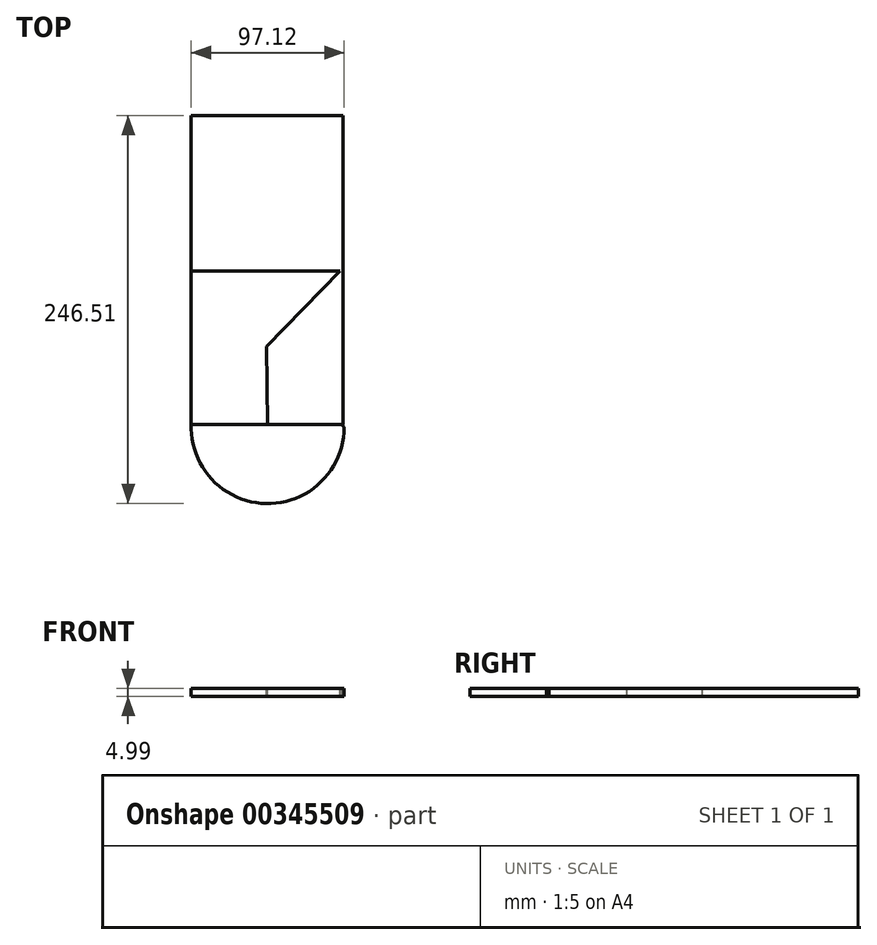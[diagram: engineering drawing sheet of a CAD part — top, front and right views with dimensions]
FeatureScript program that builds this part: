
annotation { "Feature Type Name" : "Feature", "Feature Type Description" : "" }
export const myFeature = defineFeature(function(context is Context, id is Id, definition is map)
    precondition{}
    {
        {
            var Q0;
            Q0=qCreatedBy(makeId("Top.planeOp"),FACE);
            var sketch = newSketch(context, id + "F0", { "sketchPlane" : qUnion([Q0])});
            skLineSegment(sketch, "E0.bottom", {"start": v(96.47, -97.42) * mm, "end": v(0, -97.42) * mm});
            skLineSegment(sketch, "E0.top", {"start": v(96.47, 98.96) * mm, "end": v(0, 98.96) * mm});
            skLineSegment(sketch, "E0.left", {"start": v(96.47, -97.42) * mm, "end": v(96.47, 98.96) * mm});
            skLineSegment(sketch, "E0.right", {"start": v(0, -97.42) * mm, "end": v(0, 98.96) * mm});
            skSolve(sketch);
        }
        {
            var Q0;
            Q0 = qSketchRegion(id + "F0", true);
            var sketch = newSketch(context, id + "F1", { "sketchPlane" : qUnion([Q0])});
            skArc(sketch, "E1", {"start": v(0, -96.81) * mm, "mid": v(0, -96.88) * mm, "end": v(0, -96.94) * mm});
            skLineSegment(sketch, "E2", {"start": v(94.51, 0) * mm, "end": v(0, 0) * mm});
            skLineSegment(sketch, "E3", {"start": v(0, 0) * mm, "end": v(97.07, -99.02) * mm});
            skLineSegment(sketch, "E4", {"start": v(0, -96.94) * mm, "end": v(94.51, 0) * mm});
            skLineSegment(sketch, "E5", {"start": v(47.25, 0) * mm, "end": v(48.53, -98.6) * mm});
            skPoint(sketch, "E5.startSnap0", {"position": v(47.25, -48.47) * mm});
            skPoint(sketch, "E5.endSnap0", {"position": v(48.53, -49.51) * mm});
            skArc(sketch, "E6", {"start": v(0, -96.81) * mm, "mid": v(47.4, -147.53) * mm, "end": v(97.07, -99.02) * mm});
            skSolve(sketch);
        }
        {
            var Q0;
            {var subQ2=sQuery(id+"F1.wireOp",EDGE,"E1");Q0=makeQuery(id+"F1.imprint","IMPRINT",FACE,{"disambiguationData":[TD([[makeQuery(id+"F1.imprint","IMPRINT",EDGE,{"derivedFrom":subQ2}),-1.0]])]});}
            var Q1;
            {var subQ13=makeQuery(id+"F0.imprint","IMPRINT",EDGE,{"derivedFrom":sQuery(id+"F0.wireOp",EDGE,"E0.top")});Q1=makeQuery(id+"F1.imprint","IMPRINT",FACE,{"disambiguationData":[TD([[makeQuery(id+"F1.imprint","IMPRINT",EDGE,{"derivedFrom":subQ13}),1.0]])]});}
            var Q2;
            {var subQ0=sQuery(id+"F1.wireOp",EDGE,"E5");var subQ1=sQuery(id+"F1.wireOp",EDGE,"E3");var subQ2=makeQuery(id+"F1.imprint","INTERSECT",VERTEX,{"derivedFrom":[subQ1,subQ0]});Q2=makeQuery(id+"F1.imprint","IMPRINT",FACE,{"disambiguationData":[TD([[makeQuery(id+"F1.imprint","IMPRINT",EDGE,{"disambiguationData":[TD([[subQ2,-1.0]])],"derivedFrom":subQ1}),-1.0]])]});}
            var Q3;
            Q3=makeQuery(id+"F0.imprint","IMPRINT",FACE,{"disambiguationData":[TD([[makeQuery(id+"F0.imprint","IMPRINT",EDGE,{"derivedFrom":sQuery(id+"F0.wireOp",EDGE,"E0.bottom")}),-1.0]])]});
            extrude(context, id + "F2", {"entities" : qUnion([Q0, Q1, Q2, Q3]), "oppositeDirection" : true, "depth" : 5 * mm});
        }
    });
